# Revit family: Geberit AquaClean için duvar tipi kumanda paneli_PRO_231561
name_source: partatom
category: Furniture
revit_build: Autodesk Revit 2018 (Build: 20190510_1515(x64)
units: mm (PartAtom-declared; Revit-internal decimal feet)

## family parameters
Always vertical = Yes
Cut with Voids When Loaded = No
OmniClass Number = 23.40.20.21
OmniClass Title = Toilet and Bath Specialties
Room Calculation Point = Yes
Shared = No
Work Plane-Based = No

## types (2) — shared parameters
Application purposes = Taharet sistemi fonksiyonlarının manuel ve kablosuz kontrolü için
Sıva üstü montaj için
Geberit AquaClean Tuma Comfort için
Geberit AquaClean Mera komple akıllı klozetler için
Application range = Furniture
B = 9.3 cm
BIM Content Version = GEB MG 1.2
BIM Content revision date = 2020.05.18
Brand = Geberit
CW Connection = Yes
Characteristics = Kapasitif kullanıcı arayüzü
Cam yüzey
Bluetooth üzerinden bağlantı
Zayıf pil uyarısı
Description = Geberit AquaClean için duvar tipi kumanda paneli
GEB_culture = tr-TR
GEB_generic_description = GBC
GEB_generic_manufacturer = generic
GEB_pimversion = 22.02.12
GEB_processing_type = T
GEB_reference = PRO_231561
GEB_translations = {"ATT_10673":"EAN code basic data","ATT_10931":"B","ATT_10951":"H","ATT_459792":"Renk / Yüzey","applicationPurposes":"Application purposes","application_range":"Application range","brandName":"Brand","characteristics":"Characteristics","content_creator":"BIM Content creator","content_date_changed":"BIM Content revision date","content_version":"BIM Content Version","key 1000":"Article number key","name":"Name","productBrand":"Product brand","scopeOfDelivery":"Scope of delivery","type":"Type","fixed_material":"Main material"}
H = 9.3 cm
HW Connection = No
IfcDescription = Geberit AquaClean için duvar tipi kumanda paneli
IfcExportAs = IfcUnitaryControlElement
IfcExportType = CONTROLPANEL
LOD300 = No
LOD400 = Yes
Main material = Geberit, Plastic, Opaque white
Manufacturer = Geberit
Name = Geberit AquaClean için duvar tipi kumanda paneli
Product brand = AquaClean
Scope of delivery = 3 lityum pil Type CR 2032
Sabitleme malzemesi
Vent Connection = No
Waste Connection = Yes

## per-type parameters (varying)
| type | 147038_0_0_view | 147038_0_1_view | Article number key | EAN code basic data | Renk / Yüzey |
| 147.038.SI.1 Geberit AquaClean için duvar tipi kumanda paneli | Yes | No | 147.038.SI.1 | 4025416817031 | Beyaz / Cam |
| 147.038.SJ.1 Geberit AquaClean için duvar tipi kumanda paneli | No | Yes | 147.038.SJ.1 | 4025416817048 | Siyah / Cam |

## geometry (parser evidence)
native form markers: Blend x8, Sweep x17
no freeform markers — native parametric forms only
